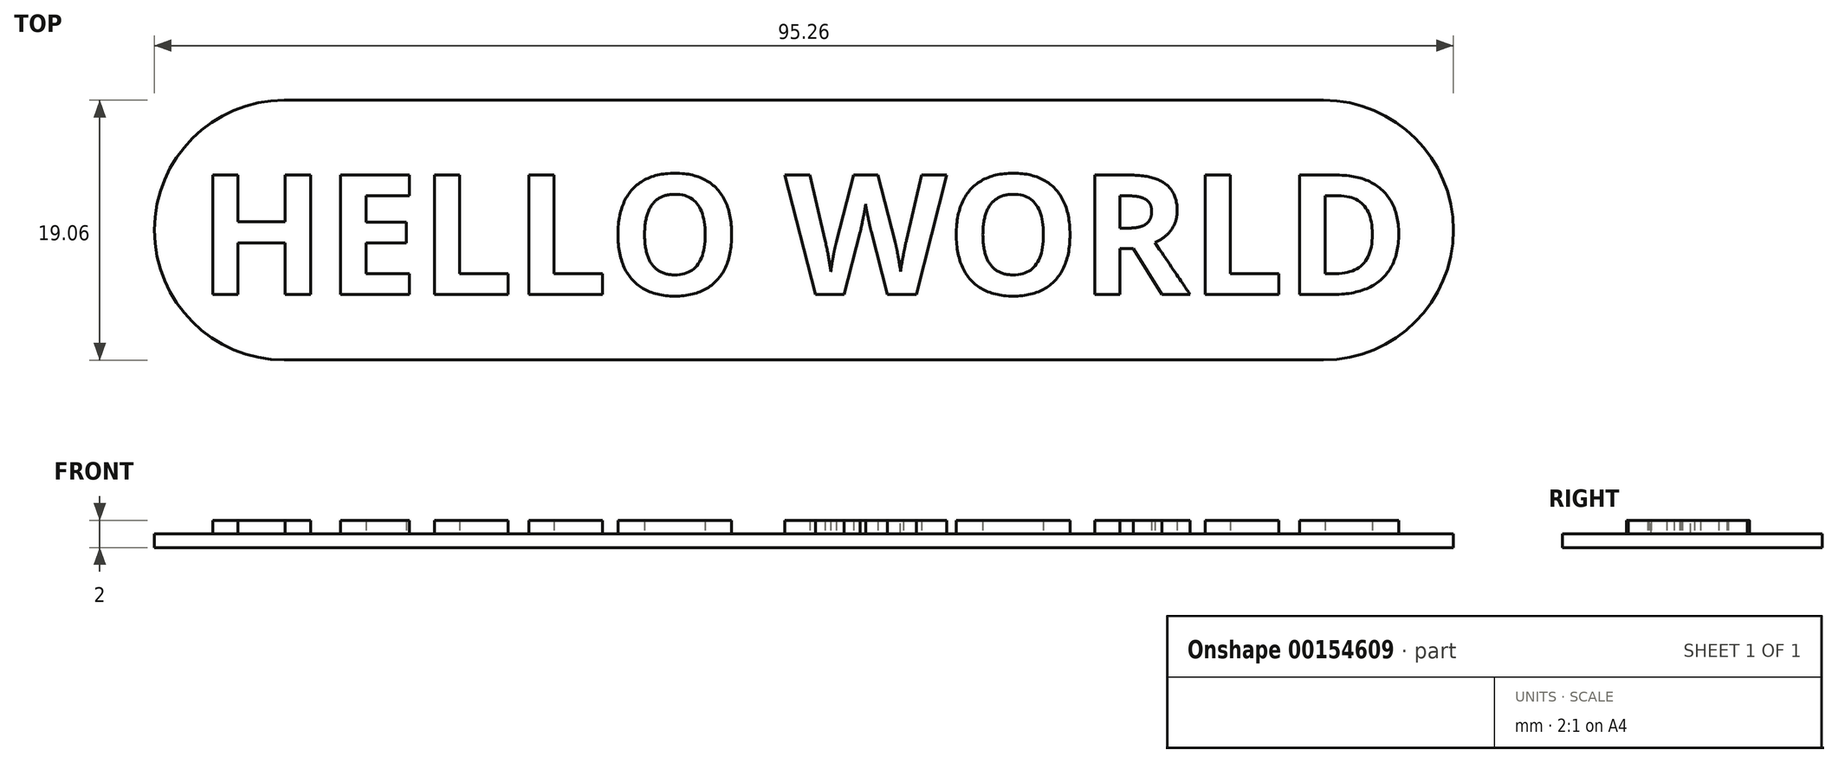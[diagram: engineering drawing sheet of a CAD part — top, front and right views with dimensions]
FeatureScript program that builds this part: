
annotation { "Feature Type Name" : "Feature", "Feature Type Description" : "" }
export const myFeature = defineFeature(function(context is Context, id is Id, definition is map)
    precondition{}
    {
        {
            var Q0;
            Q0=qCreatedBy(makeId("Top.planeOp"),FACE);
            var sketch = newSketch(context, id + "F0", { "sketchPlane" : qUnion([Q0])});
            skLineSegment(sketch, "E0.bottom", {"start": v(47.63, 9.53) * mm, "end": v(-47.62, 9.53) * mm});
            skLineSegment(sketch, "E0.top", {"start": v(47.62, -9.53) * mm, "end": v(-47.63, -9.53) * mm});
            skLineSegment(sketch, "E0.left", {"start": v(47.63, 9.53) * mm, "end": v(47.62, -9.53) * mm});
            skLineSegment(sketch, "E0.right", {"start": v(-47.62, 9.53) * mm, "end": v(-47.63, -9.53) * mm});
            skPoint(sketch, "E0.middle", {"position": v(0, 0) * mm});
            skSolve(sketch);
        }
        {
            var Q0;
            Q0=qCreatedBy(makeId("Top.planeOp"),FACE);
            var sketch = newSketch(context, id + "F1", { "sketchPlane" : qUnion([Q0])});
            skText(sketch, "E1", { "text": "HELLO WORLD", "fontName": "OpenSans-Bold.ttf"});
            const initialGuessF1  = {"E1": [-0.04445, -0.00472, 1, 0, 0.00883]};
            skSetInitialGuess(sketch, initialGuessF1);
            skSolve(sketch);
        }
        {
            var Q0;
            Q0 = qSketchRegion(id + "F0", true);
            extrude(context, id + "F2", {"entities" : qUnion([Q0]), "depth" : 1 * mm});
        }
        {
            var Q0;
            Q0 = qSketchRegion(id + "F1", true);
            extrude(context, id + "F3", {"entities" : qUnion([Q0]), "operationType" : NewBodyOperationType.ADD, "depth" : 2 * mm});
        }
        {
            var Q0;
            Q0=makeQuery(id+"F2.opExtrude","SWEPT_EDGE",EDGE,{"disambiguationData":[OSD([sQuery(id+"F0.wireOp",EDGE,"E0.bottom"),sQuery(id+"F0.wireOp",EDGE,"E0.right")])]});
            var Q1;
            Q1=makeQuery(id+"F2.opExtrude","SWEPT_EDGE",EDGE,{"disambiguationData":[OSD([sQuery(id+"F0.wireOp",EDGE,"E0.top"),sQuery(id+"F0.wireOp",EDGE,"E0.left")])]});
            var Q2;
            Q2=makeQuery(id+"F2.opExtrude","SWEPT_EDGE",EDGE,{"disambiguationData":[OSD([sQuery(id+"F0.wireOp",EDGE,"E0.top"),sQuery(id+"F0.wireOp",EDGE,"E0.right")])]});
            var Q3;
            Q3=makeQuery(id+"F2.opExtrude","SWEPT_EDGE",EDGE,{"disambiguationData":[OSD([sQuery(id+"F0.wireOp",EDGE,"E0.bottom"),sQuery(id+"F0.wireOp",EDGE,"E0.left")])]});
            fillet(context, id + "F4", {"entities" : qUnion([Q0, Q1, Q2, Q3]), "radius" : 9.52 * mm, "tangentPropagation" : true, "allowEdgeOverflow" : false});
        }
    });
